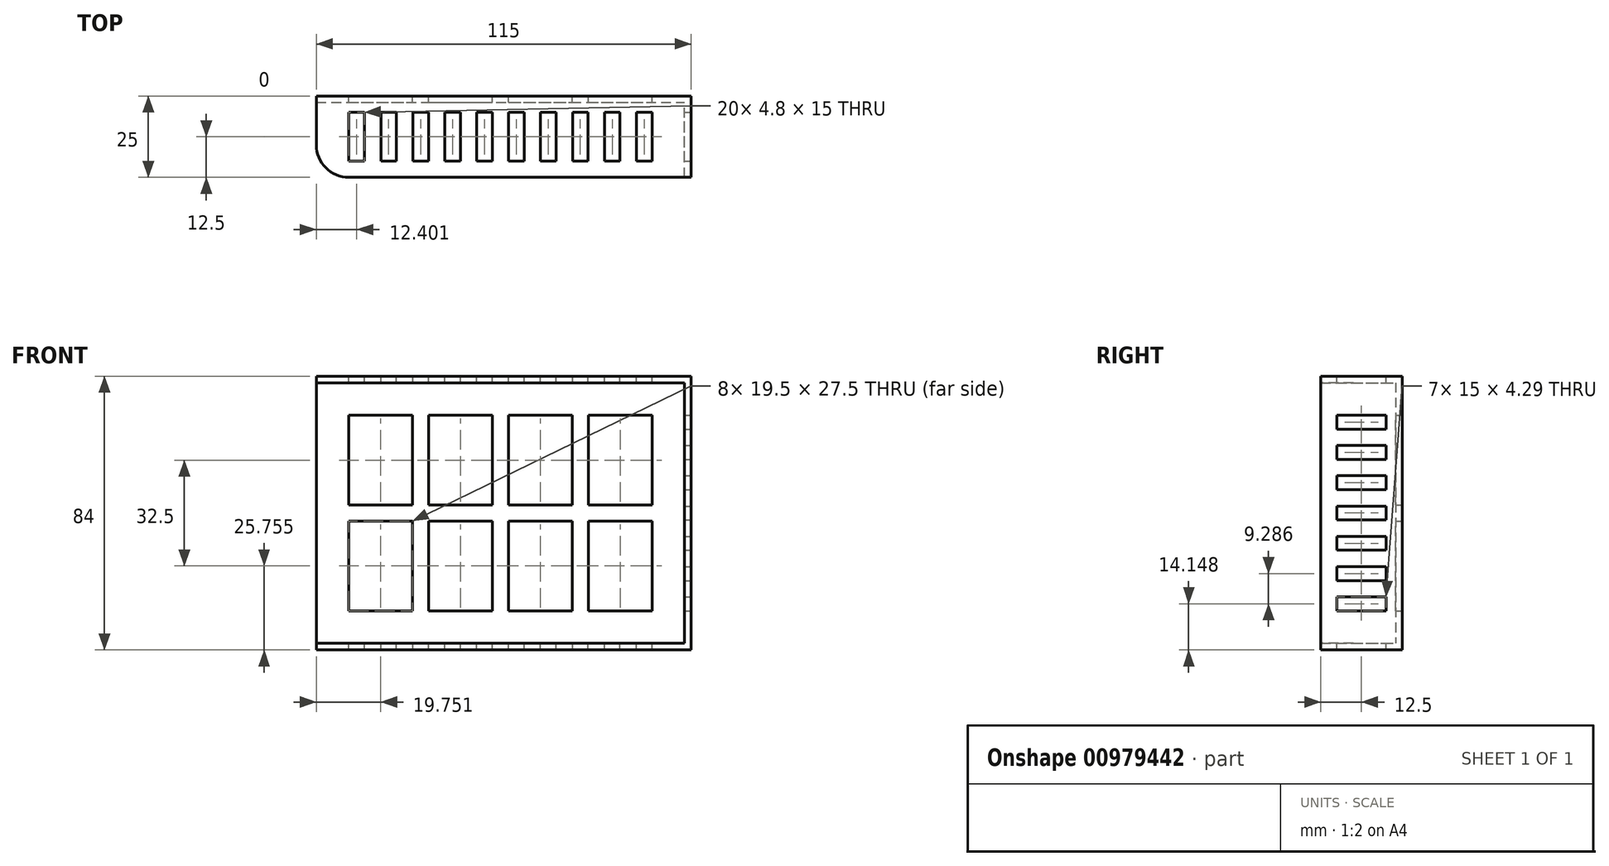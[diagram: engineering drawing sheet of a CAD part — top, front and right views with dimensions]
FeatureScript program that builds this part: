
annotation { "Feature Type Name" : "Feature", "Feature Type Description" : "" }
export const myFeature = defineFeature(function(context is Context, id is Id, definition is map)
    precondition{}
    {
        {
            var Q0;
            Q0=qCreatedBy(makeId("Front.planeOp"),FACE);
            var sketch = newSketch(context, id + "F0", { "sketchPlane" : qUnion([Q0])});
            skLineSegment(sketch, "E0.bottom", {"start": v(-149.44, 24.07) * mm, "end": v(-34.44, 24.07) * mm});
            skLineSegment(sketch, "E0.top", {"start": v(-149.44, -59.93) * mm, "end": v(-34.44, -59.93) * mm});
            skLineSegment(sketch, "E0.left", {"start": v(-149.44, 24.07) * mm, "end": v(-149.44, -59.93) * mm});
            skLineSegment(sketch, "E0.right", {"start": v(-34.44, 24.07) * mm, "end": v(-34.44, -59.93) * mm});
            skSolve(sketch);
        }
        {
            var Q0;
            Q0=makeQuery(id+"F0.imprint","IMPRINT",FACE,{"disambiguationData":[TD([[makeQuery(id+"F0.imprint","IMPRINT",EDGE,{"derivedFrom":sQuery(id+"F0.wireOp",EDGE,"E0.bottom")}),-1.0]])]});
            extrude(context, id + "F1", {"entities" : qUnion([Q0]), "depth" : 25 * mm, "offsetDistance" : 25 * mm});
        }
        {
            var Q0;
            Q0=makeQuery(id+"F1.opExtrude","CAP_FACE",FACE,{"disambiguationData":[OSD([sQuery(id+"F0.wireOp",EDGE,"E0.bottom"),sQuery(id+"F0.wireOp",EDGE,"E0.top"),sQuery(id+"F0.wireOp",EDGE,"E0.left"),sQuery(id+"F0.wireOp",EDGE,"E0.right")])],"isStart":false});
            var Q1;
            Q1=makeQuery(id+"F1.opExtrude","SWEPT_FACE",FACE,{"disambiguationData":[OSD([sQuery(id+"F0.wireOp",EDGE,"E0.left")])]});
            shell(context, id + "F2", {"entities" : qUnion([Q0, Q1]), "thickness" : 2 * mm});
        }
        {
            var Q0;
            Q0=makeQuery(id+"F1.opExtrude","CAP_EDGE",EDGE,{"disambiguationData":[OSD([sQuery(id+"F0.wireOp",EDGE,"E0.left")])],"isStart":false});
            var Q1;
            {var subQ0=sQuery(id+"F0.wireOp",EDGE,"E0.left");Q1=makeQuery(id+"F2.opShell","OFFSET_EDGE",EDGE,{"disambiguationData":[OSD([subQ0]),TDD([makeQuery(id+"F1.opExtrude","CAP_EDGE",EDGE,{"disambiguationData":[OSD([subQ0])],"isStart":false})])]});}
            fillet(context, id + "F3", {"entities" : qUnion([Q0, Q1]), "radius" : 10 * mm, "tangentPropagation" : true, "allowEdgeOverflow" : false});
        }
        {
            var Q0;
            Q0=makeQuery(id+"F1.opExtrude","CAP_FACE",FACE,{"disambiguationData":[OSD([sQuery(id+"F0.wireOp",EDGE,"E0.bottom"),sQuery(id+"F0.wireOp",EDGE,"E0.top"),sQuery(id+"F0.wireOp",EDGE,"E0.left"),sQuery(id+"F0.wireOp",EDGE,"E0.right")])],"isStart":true});
            var sketch = newSketch(context, id + "F4", { "sketchPlane" : qUnion([Q0])});
            skLineSegment(sketch, "E1.bottom", {"start": v(46.44, 12.07) * mm, "end": v(65.94, 12.07) * mm});
            skLineSegment(sketch, "E1.top", {"start": v(46.44, -15.43) * mm, "end": v(65.94, -15.43) * mm});
            skLineSegment(sketch, "E1.left", {"start": v(46.44, 12.07) * mm, "end": v(46.44, -15.43) * mm});
            skLineSegment(sketch, "E1.right", {"start": v(65.94, 12.07) * mm, "end": v(65.94, -15.43) * mm});
            skLineSegment(sketch, "E2.0.1.0", {"start": v(46.44, -20.43) * mm, "end": v(65.94, -20.43) * mm});
            skLineSegment(sketch, "E2.0.1.1", {"start": v(65.94, -20.43) * mm, "end": v(65.94, -47.93) * mm});
            skLineSegment(sketch, "E2.0.1.2", {"start": v(46.44, -47.93) * mm, "end": v(65.94, -47.93) * mm});
            skLineSegment(sketch, "E2.0.1.3", {"start": v(46.44, -20.43) * mm, "end": v(46.44, -47.93) * mm});
            skLineSegment(sketch, "E2.1.0.0", {"start": v(70.94, 12.07) * mm, "end": v(90.44, 12.07) * mm});
            skLineSegment(sketch, "E2.1.0.1", {"start": v(90.44, 12.07) * mm, "end": v(90.44, -15.43) * mm});
            skLineSegment(sketch, "E2.1.0.2", {"start": v(70.94, -15.43) * mm, "end": v(90.44, -15.43) * mm});
            skLineSegment(sketch, "E2.1.0.3", {"start": v(70.94, 12.07) * mm, "end": v(70.94, -15.43) * mm});
            skLineSegment(sketch, "E2.1.1.0", {"start": v(70.94, -20.43) * mm, "end": v(90.44, -20.43) * mm});
            skLineSegment(sketch, "E2.1.1.1", {"start": v(90.44, -20.43) * mm, "end": v(90.44, -47.93) * mm});
            skLineSegment(sketch, "E2.1.1.2", {"start": v(70.94, -47.93) * mm, "end": v(90.44, -47.93) * mm});
            skLineSegment(sketch, "E2.1.1.3", {"start": v(70.94, -20.43) * mm, "end": v(70.94, -47.93) * mm});
            skLineSegment(sketch, "E2.2.0.0", {"start": v(95.44, 12.07) * mm, "end": v(114.94, 12.07) * mm});
            skLineSegment(sketch, "E2.2.0.1", {"start": v(114.94, 12.07) * mm, "end": v(114.94, -15.43) * mm});
            skLineSegment(sketch, "E2.2.0.2", {"start": v(95.44, -15.43) * mm, "end": v(114.94, -15.43) * mm});
            skLineSegment(sketch, "E2.2.0.3", {"start": v(95.44, 12.07) * mm, "end": v(95.44, -15.43) * mm});
            skLineSegment(sketch, "E2.2.1.0", {"start": v(95.44, -20.43) * mm, "end": v(114.94, -20.43) * mm});
            skLineSegment(sketch, "E2.2.1.1", {"start": v(114.94, -20.43) * mm, "end": v(114.94, -47.93) * mm});
            skLineSegment(sketch, "E2.2.1.2", {"start": v(95.44, -47.93) * mm, "end": v(114.94, -47.93) * mm});
            skLineSegment(sketch, "E2.2.1.3", {"start": v(95.44, -20.43) * mm, "end": v(95.44, -47.93) * mm});
            skLineSegment(sketch, "E2.3.0.0", {"start": v(119.94, 12.07) * mm, "end": v(139.44, 12.07) * mm});
            skLineSegment(sketch, "E2.3.0.1", {"start": v(139.44, 12.07) * mm, "end": v(139.44, -15.43) * mm});
            skLineSegment(sketch, "E2.3.0.2", {"start": v(119.94, -15.43) * mm, "end": v(139.44, -15.43) * mm});
            skLineSegment(sketch, "E2.3.0.3", {"start": v(119.94, 12.07) * mm, "end": v(119.94, -15.43) * mm});
            skLineSegment(sketch, "E2.3.1.0", {"start": v(119.94, -20.43) * mm, "end": v(139.44, -20.43) * mm});
            skLineSegment(sketch, "E2.3.1.1", {"start": v(139.44, -20.43) * mm, "end": v(139.44, -47.93) * mm});
            skLineSegment(sketch, "E2.3.1.2", {"start": v(119.94, -47.93) * mm, "end": v(139.44, -47.93) * mm});
            skLineSegment(sketch, "E2.3.1.3", {"start": v(119.94, -20.43) * mm, "end": v(119.94, -47.93) * mm});
            skLineSegment(sketch, "E2.direction1", {"start": v(46.44, 12.07) * mm, "end": v(70.94, 12.07) * mm, "construction": true});
            skLineSegment(sketch, "E2.direction2", {"start": v(46.44, 12.07) * mm, "end": v(46.44, -20.43) * mm, "construction": true});
            skSolve(sketch);
        }
        {
            var Q0;
            Q0=makeQuery(id+"F4.imprint","IMPRINT",FACE,{"disambiguationData":[TD([[makeQuery(id+"F4.imprint","IMPRINT",EDGE,{"derivedFrom":sQuery(id+"F4.wireOp",EDGE,"E1.bottom")}),-1.0]])]});
            var Q1;
            Q1=makeQuery(id+"F4.imprint","IMPRINT",FACE,{"disambiguationData":[TD([[makeQuery(id+"F4.imprint","IMPRINT",EDGE,{"derivedFrom":sQuery(id+"F4.wireOp",EDGE,"E2.1.0.0")}),-1.0]])]});
            var Q2;
            Q2=makeQuery(id+"F4.imprint","IMPRINT",FACE,{"disambiguationData":[TD([[makeQuery(id+"F4.imprint","IMPRINT",EDGE,{"derivedFrom":sQuery(id+"F4.wireOp",EDGE,"E2.2.0.0")}),-1.0]])]});
            var Q3;
            Q3=makeQuery(id+"F4.imprint","IMPRINT",FACE,{"disambiguationData":[TD([[makeQuery(id+"F4.imprint","IMPRINT",EDGE,{"derivedFrom":sQuery(id+"F4.wireOp",EDGE,"E2.3.0.0")}),-1.0]])]});
            var Q4;
            Q4=makeQuery(id+"F4.imprint","IMPRINT",FACE,{"disambiguationData":[TD([[makeQuery(id+"F4.imprint","IMPRINT",EDGE,{"derivedFrom":sQuery(id+"F4.wireOp",EDGE,"E2.3.1.0")}),-1.0]])]});
            var Q5;
            Q5=makeQuery(id+"F4.imprint","IMPRINT",FACE,{"disambiguationData":[TD([[makeQuery(id+"F4.imprint","IMPRINT",EDGE,{"derivedFrom":sQuery(id+"F4.wireOp",EDGE,"E2.2.1.0")}),-1.0]])]});
            var Q6;
            Q6=makeQuery(id+"F4.imprint","IMPRINT",FACE,{"disambiguationData":[TD([[makeQuery(id+"F4.imprint","IMPRINT",EDGE,{"derivedFrom":sQuery(id+"F4.wireOp",EDGE,"E2.1.1.0")}),-1.0]])]});
            var Q7;
            Q7=makeQuery(id+"F4.imprint","IMPRINT",FACE,{"disambiguationData":[TD([[makeQuery(id+"F4.imprint","IMPRINT",EDGE,{"derivedFrom":sQuery(id+"F4.wireOp",EDGE,"E2.0.1.0")}),-1.0]])]});
            extrude(context, id + "F5", {"entities" : qUnion([Q0, Q1, Q2, Q3, Q4, Q5, Q6, Q7]), "operationType" : NewBodyOperationType.REMOVE, "oppositeDirection" : true, "depth" : 25 * mm, "offsetDistance" : 25 * mm});
        }
        {
            var Q0;
            Q0=makeQuery(id+"F1.opExtrude","SWEPT_FACE",FACE,{"disambiguationData":[OSD([sQuery(id+"F0.wireOp",EDGE,"E0.bottom")])]});
            var sketch = newSketch(context, id + "F6", { "sketchPlane" : qUnion([Q0])});
            skLineSegment(sketch, "E3.bottom", {"start": v(-46.44, -20) * mm, "end": v(-51.24, -20) * mm});
            skLineSegment(sketch, "E3.top", {"start": v(-46.44, -5) * mm, "end": v(-51.24, -5) * mm});
            skLineSegment(sketch, "E3.left", {"start": v(-46.44, -20) * mm, "end": v(-46.44, -5) * mm});
            skLineSegment(sketch, "E3.right", {"start": v(-51.24, -20) * mm, "end": v(-51.24, -5) * mm});
            skLineSegment(sketch, "E4.1.0.0", {"start": v(-61.04, -20) * mm, "end": v(-61.04, -5) * mm});
            skLineSegment(sketch, "E4.1.0.1", {"start": v(-56.24, -20) * mm, "end": v(-61.04, -20) * mm});
            skLineSegment(sketch, "E4.1.0.2", {"start": v(-56.24, -20) * mm, "end": v(-56.24, -5) * mm});
            skLineSegment(sketch, "E4.1.0.3", {"start": v(-56.24, -5) * mm, "end": v(-61.04, -5) * mm});
            skLineSegment(sketch, "E4.2.0.0", {"start": v(-70.84, -20) * mm, "end": v(-70.84, -5) * mm});
            skLineSegment(sketch, "E4.2.0.1", {"start": v(-66.04, -20) * mm, "end": v(-70.84, -20) * mm});
            skLineSegment(sketch, "E4.2.0.2", {"start": v(-66.04, -20) * mm, "end": v(-66.04, -5) * mm});
            skLineSegment(sketch, "E4.2.0.3", {"start": v(-66.04, -5) * mm, "end": v(-70.84, -5) * mm});
            skLineSegment(sketch, "E4.3.0.0", {"start": v(-80.64, -20) * mm, "end": v(-80.64, -5) * mm});
            skLineSegment(sketch, "E4.3.0.1", {"start": v(-75.84, -20) * mm, "end": v(-80.64, -20) * mm});
            skLineSegment(sketch, "E4.3.0.2", {"start": v(-75.84, -20) * mm, "end": v(-75.84, -5) * mm});
            skLineSegment(sketch, "E4.3.0.3", {"start": v(-75.84, -5) * mm, "end": v(-80.64, -5) * mm});
            skLineSegment(sketch, "E4.4.0.0", {"start": v(-90.44, -20) * mm, "end": v(-90.44, -5) * mm});
            skLineSegment(sketch, "E4.4.0.1", {"start": v(-85.64, -20) * mm, "end": v(-90.44, -20) * mm});
            skLineSegment(sketch, "E4.4.0.2", {"start": v(-85.64, -20) * mm, "end": v(-85.64, -5) * mm});
            skLineSegment(sketch, "E4.4.0.3", {"start": v(-85.64, -5) * mm, "end": v(-90.44, -5) * mm});
            skLineSegment(sketch, "E4.5.0.0", {"start": v(-100.24, -20) * mm, "end": v(-100.24, -5) * mm});
            skLineSegment(sketch, "E4.5.0.1", {"start": v(-95.44, -20) * mm, "end": v(-100.24, -20) * mm});
            skLineSegment(sketch, "E4.5.0.2", {"start": v(-95.44, -20) * mm, "end": v(-95.44, -5) * mm});
            skLineSegment(sketch, "E4.5.0.3", {"start": v(-95.44, -5) * mm, "end": v(-100.24, -5) * mm});
            skLineSegment(sketch, "E4.6.0.0", {"start": v(-110.04, -20) * mm, "end": v(-110.04, -5) * mm});
            skLineSegment(sketch, "E4.6.0.1", {"start": v(-105.24, -20) * mm, "end": v(-110.04, -20) * mm});
            skLineSegment(sketch, "E4.6.0.2", {"start": v(-105.24, -20) * mm, "end": v(-105.24, -5) * mm});
            skLineSegment(sketch, "E4.6.0.3", {"start": v(-105.24, -5) * mm, "end": v(-110.04, -5) * mm});
            skLineSegment(sketch, "E4.7.0.0", {"start": v(-119.84, -20) * mm, "end": v(-119.84, -5) * mm});
            skLineSegment(sketch, "E4.7.0.1", {"start": v(-115.04, -20) * mm, "end": v(-119.84, -20) * mm});
            skLineSegment(sketch, "E4.7.0.2", {"start": v(-115.04, -20) * mm, "end": v(-115.04, -5) * mm});
            skLineSegment(sketch, "E4.7.0.3", {"start": v(-115.04, -5) * mm, "end": v(-119.84, -5) * mm});
            skLineSegment(sketch, "E4.8.0.0", {"start": v(-129.64, -20) * mm, "end": v(-129.64, -5) * mm});
            skLineSegment(sketch, "E4.8.0.1", {"start": v(-124.84, -20) * mm, "end": v(-129.64, -20) * mm});
            skLineSegment(sketch, "E4.8.0.2", {"start": v(-124.84, -20) * mm, "end": v(-124.84, -5) * mm});
            skLineSegment(sketch, "E4.8.0.3", {"start": v(-124.84, -5) * mm, "end": v(-129.64, -5) * mm});
            skLineSegment(sketch, "E4.9.0.0", {"start": v(-139.44, -20) * mm, "end": v(-139.44, -5) * mm});
            skLineSegment(sketch, "E4.9.0.1", {"start": v(-134.64, -20) * mm, "end": v(-139.44, -20) * mm});
            skLineSegment(sketch, "E4.9.0.2", {"start": v(-134.64, -20) * mm, "end": v(-134.64, -5) * mm});
            skLineSegment(sketch, "E4.9.0.3", {"start": v(-134.64, -5) * mm, "end": v(-139.44, -5) * mm});
            skLineSegment(sketch, "E4.direction1", {"start": v(-51.24, -20) * mm, "end": v(-61.04, -20) * mm, "construction": true});
            skPoint(sketch, "E5.right.end.orphan", {"position": v(-139.44, -5) * mm});
            skSolve(sketch);
        }
        {
            var Q0;
            Q0=makeQuery(id+"F6.imprint","IMPRINT",FACE,{"disambiguationData":[TD([[makeQuery(id+"F6.imprint","IMPRINT",EDGE,{"derivedFrom":sQuery(id+"F6.wireOp",EDGE,"E3.bottom")}),-1.0]])]});
            var Q1;
            Q1=makeQuery(id+"F6.imprint","IMPRINT",FACE,{"disambiguationData":[TD([[makeQuery(id+"F6.imprint","IMPRINT",EDGE,{"derivedFrom":sQuery(id+"F6.wireOp",EDGE,"E4.1.0.0")}),-1.0]])]});
            var Q2;
            Q2=makeQuery(id+"F6.imprint","IMPRINT",FACE,{"disambiguationData":[TD([[makeQuery(id+"F6.imprint","IMPRINT",EDGE,{"derivedFrom":sQuery(id+"F6.wireOp",EDGE,"E4.2.0.0")}),-1.0]])]});
            var Q3;
            Q3=makeQuery(id+"F6.imprint","IMPRINT",FACE,{"disambiguationData":[TD([[makeQuery(id+"F6.imprint","IMPRINT",EDGE,{"derivedFrom":sQuery(id+"F6.wireOp",EDGE,"E4.3.0.0")}),-1.0]])]});
            var Q4;
            Q4=makeQuery(id+"F6.imprint","IMPRINT",FACE,{"disambiguationData":[TD([[makeQuery(id+"F6.imprint","IMPRINT",EDGE,{"derivedFrom":sQuery(id+"F6.wireOp",EDGE,"E4.4.0.0")}),-1.0]])]});
            var Q5;
            Q5=makeQuery(id+"F6.imprint","IMPRINT",FACE,{"disambiguationData":[TD([[makeQuery(id+"F6.imprint","IMPRINT",EDGE,{"derivedFrom":sQuery(id+"F6.wireOp",EDGE,"E4.5.0.0")}),-1.0]])]});
            var Q6;
            Q6=makeQuery(id+"F6.imprint","IMPRINT",FACE,{"disambiguationData":[TD([[makeQuery(id+"F6.imprint","IMPRINT",EDGE,{"derivedFrom":sQuery(id+"F6.wireOp",EDGE,"E4.6.0.0")}),-1.0]])]});
            var Q7;
            Q7=makeQuery(id+"F6.imprint","IMPRINT",FACE,{"disambiguationData":[TD([[makeQuery(id+"F6.imprint","IMPRINT",EDGE,{"derivedFrom":sQuery(id+"F6.wireOp",EDGE,"E4.7.0.0")}),-1.0]])]});
            var Q8;
            Q8=makeQuery(id+"F6.imprint","IMPRINT",FACE,{"disambiguationData":[TD([[makeQuery(id+"F6.imprint","IMPRINT",EDGE,{"derivedFrom":sQuery(id+"F6.wireOp",EDGE,"E4.8.0.0")}),-1.0]])]});
            var Q9;
            Q9=makeQuery(id+"F6.imprint","IMPRINT",FACE,{"disambiguationData":[TD([[makeQuery(id+"F6.imprint","IMPRINT",EDGE,{"derivedFrom":sQuery(id+"F6.wireOp",EDGE,"E4.9.0.0")}),-1.0]])]});
            extrude(context, id + "F7", {"entities" : qUnion([Q0, Q1, Q2, Q3, Q4, Q5, Q6, Q7, Q8, Q9]), "operationType" : NewBodyOperationType.REMOVE, "endBound" : BoundingType.THROUGH_ALL, "oppositeDirection" : true, "depth" : 25 * mm, "offsetDistance" : 25 * mm});
        }
        {
            var Q0;
            Q0=makeQuery(id+"F1.opExtrude","SWEPT_FACE",FACE,{"disambiguationData":[OSD([sQuery(id+"F0.wireOp",EDGE,"E0.right")])]});
            var sketch = newSketch(context, id + "F8", { "sketchPlane" : qUnion([Q0])});
            skLineSegment(sketch, "E6.bottom", {"start": v(-20, -47.93) * mm, "end": v(-5, -47.93) * mm});
            skLineSegment(sketch, "E6.top", {"start": v(-20, -43.64) * mm, "end": v(-5, -43.64) * mm});
            skLineSegment(sketch, "E6.left", {"start": v(-20, -47.93) * mm, "end": v(-20, -43.64) * mm});
            skLineSegment(sketch, "E6.right", {"start": v(-5, -47.93) * mm, "end": v(-5, -43.64) * mm});
            skLineSegment(sketch, "E7.0.1.0", {"start": v(-20, -34.35) * mm, "end": v(-5, -34.35) * mm});
            skLineSegment(sketch, "E7.0.1.1", {"start": v(-20, -38.64) * mm, "end": v(-20, -34.35) * mm});
            skLineSegment(sketch, "E7.0.1.2", {"start": v(-20, -38.64) * mm, "end": v(-5, -38.64) * mm});
            skLineSegment(sketch, "E7.0.1.3", {"start": v(-5, -38.64) * mm, "end": v(-5, -34.35) * mm});
            skLineSegment(sketch, "E7.0.2.0", {"start": v(-20, -25.07) * mm, "end": v(-5, -25.07) * mm});
            skLineSegment(sketch, "E7.0.2.1", {"start": v(-20, -29.35) * mm, "end": v(-20, -25.07) * mm});
            skLineSegment(sketch, "E7.0.2.2", {"start": v(-20, -29.35) * mm, "end": v(-5, -29.35) * mm});
            skLineSegment(sketch, "E7.0.2.3", {"start": v(-5, -29.35) * mm, "end": v(-5, -25.07) * mm});
            skLineSegment(sketch, "E7.0.3.0", {"start": v(-20, -15.78) * mm, "end": v(-5, -15.78) * mm});
            skLineSegment(sketch, "E7.0.3.1", {"start": v(-20, -20.07) * mm, "end": v(-20, -15.78) * mm});
            skLineSegment(sketch, "E7.0.3.2", {"start": v(-20, -20.07) * mm, "end": v(-5, -20.07) * mm});
            skLineSegment(sketch, "E7.0.3.3", {"start": v(-5, -20.07) * mm, "end": v(-5, -15.78) * mm});
            skLineSegment(sketch, "E7.0.4.0", {"start": v(-20, -6.5) * mm, "end": v(-5, -6.5) * mm});
            skLineSegment(sketch, "E7.0.4.1", {"start": v(-20, -10.78) * mm, "end": v(-20, -6.5) * mm});
            skLineSegment(sketch, "E7.0.4.2", {"start": v(-20, -10.78) * mm, "end": v(-5, -10.78) * mm});
            skLineSegment(sketch, "E7.0.4.3", {"start": v(-5, -10.78) * mm, "end": v(-5, -6.5) * mm});
            skLineSegment(sketch, "E7.0.5.0", {"start": v(-20, 2.79) * mm, "end": v(-5, 2.79) * mm});
            skLineSegment(sketch, "E7.0.5.1", {"start": v(-20, -1.5) * mm, "end": v(-20, 2.79) * mm});
            skLineSegment(sketch, "E7.0.5.2", {"start": v(-20, -1.5) * mm, "end": v(-5, -1.5) * mm});
            skLineSegment(sketch, "E7.0.5.3", {"start": v(-5, -1.5) * mm, "end": v(-5, 2.79) * mm});
            skLineSegment(sketch, "E7.0.6.0", {"start": v(-20, 12.08) * mm, "end": v(-5, 12.08) * mm});
            skLineSegment(sketch, "E7.0.6.1", {"start": v(-20, 7.79) * mm, "end": v(-20, 12.08) * mm});
            skLineSegment(sketch, "E7.0.6.2", {"start": v(-20, 7.79) * mm, "end": v(-5, 7.79) * mm});
            skLineSegment(sketch, "E7.0.6.3", {"start": v(-5, 7.79) * mm, "end": v(-5, 12.08) * mm});
            skLineSegment(sketch, "E7.direction1", {"start": v(-20, -42.93) * mm, "end": v(5, -42.93) * mm, "construction": true});
            skLineSegment(sketch, "E7.direction2", {"start": v(-20, -42.93) * mm, "end": v(-20, -33.64) * mm, "construction": true});
            skPoint(sketch, "E8.top.end.orphan", {"position": v(-5, 12.07) * mm});
            skSolve(sketch);
        }
        {
            var Q0;
            Q0=makeQuery(id+"F8.imprint","IMPRINT",FACE,{"disambiguationData":[TD([[makeQuery(id+"F8.imprint","IMPRINT",EDGE,{"derivedFrom":sQuery(id+"F8.wireOp",EDGE,"E6.bottom")}),1.0]])]});
            var Q1;
            Q1=makeQuery(id+"F8.imprint","IMPRINT",FACE,{"disambiguationData":[TD([[makeQuery(id+"F8.imprint","IMPRINT",EDGE,{"derivedFrom":sQuery(id+"F8.wireOp",EDGE,"E7.0.1.0")}),-1.0]])]});
            var Q2;
            Q2=makeQuery(id+"F8.imprint","IMPRINT",FACE,{"disambiguationData":[TD([[makeQuery(id+"F8.imprint","IMPRINT",EDGE,{"derivedFrom":sQuery(id+"F8.wireOp",EDGE,"E7.0.2.0")}),-1.0]])]});
            var Q3;
            Q3=makeQuery(id+"F8.imprint","IMPRINT",FACE,{"disambiguationData":[TD([[makeQuery(id+"F8.imprint","IMPRINT",EDGE,{"derivedFrom":sQuery(id+"F8.wireOp",EDGE,"E7.0.3.0")}),-1.0]])]});
            var Q4;
            Q4=makeQuery(id+"F8.imprint","IMPRINT",FACE,{"disambiguationData":[TD([[makeQuery(id+"F8.imprint","IMPRINT",EDGE,{"derivedFrom":sQuery(id+"F8.wireOp",EDGE,"E7.0.4.0")}),-1.0]])]});
            var Q5;
            Q5=makeQuery(id+"F8.imprint","IMPRINT",FACE,{"disambiguationData":[TD([[makeQuery(id+"F8.imprint","IMPRINT",EDGE,{"derivedFrom":sQuery(id+"F8.wireOp",EDGE,"E7.0.5.0")}),-1.0]])]});
            var Q6;
            Q6=makeQuery(id+"F8.imprint","IMPRINT",FACE,{"disambiguationData":[TD([[makeQuery(id+"F8.imprint","IMPRINT",EDGE,{"derivedFrom":sQuery(id+"F8.wireOp",EDGE,"E7.0.6.0")}),-1.0]])]});
            extrude(context, id + "F9", {"entities" : qUnion([Q0, Q1, Q2, Q3, Q4, Q5, Q6]), "operationType" : NewBodyOperationType.REMOVE, "oppositeDirection" : true, "depth" : 25 * mm, "offsetDistance" : 25 * mm});
        }
    });
